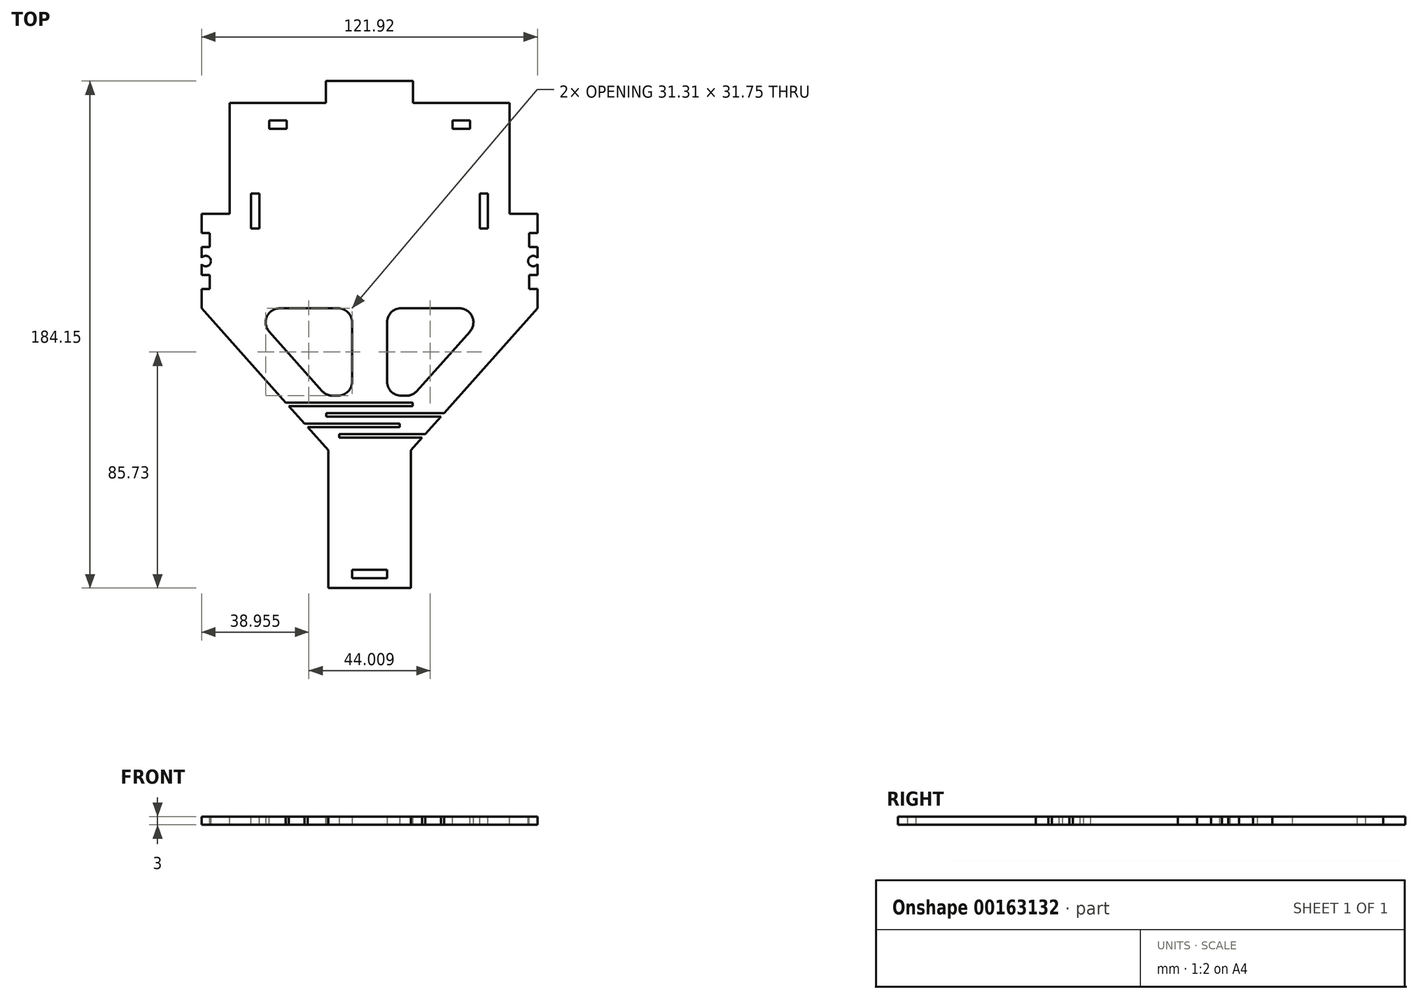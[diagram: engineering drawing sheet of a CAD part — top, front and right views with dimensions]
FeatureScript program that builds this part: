
annotation { "Feature Type Name" : "Feature", "Feature Type Description" : "" }
export const myFeature = defineFeature(function(context is Context, id is Id, definition is map)
    precondition{}
    {
        {
            var Q0;
            Q0=qCreatedBy(makeId("Top.planeOp"),FACE);
            var sketch = newSketch(context, id + "F0", { "sketchPlane" : qUnion([Q0])});
            skLineSegment(sketch, "E0.bottom", {"start": v(-50.8, 41.28) * mm, "end": v(50.8, 41.28) * mm});
            skLineSegment(sketch, "E0.top", {"start": v(-43.95, -41.28) * mm, "end": v(-6.35, -41.28) * mm});
            skLineSegment(sketch, "E0.left", {"start": v(-50.8, 41.28) * mm, "end": v(-50.8, -6.99) * mm});
            skLineSegment(sketch, "E0.right", {"start": v(50.8, 41.28) * mm, "end": v(50.8, -6.99) * mm});
            skPoint(sketch, "E0.middle", {"position": v(0, 0) * mm});
            skLineSegment(sketch, "E1.0", {"start": v(60.96, -6.98) * mm, "end": v(60.96, -41.28) * mm});
            skLineSegment(sketch, "E2.0", {"start": v(-50.8, -6.98) * mm, "end": v(50.8, -6.98) * mm, "construction": true});
            skLineSegment(sketch, "E3", {"start": v(50.8, -6.98) * mm, "end": v(60.96, -6.98) * mm});
            skPoint(sketch, "E4.orphan", {"position": v(50.8, -41.28) * mm});
            skLineSegment(sketch, "E5", {"start": v(-50.8, -6.98) * mm, "end": v(-60.96, -6.98) * mm});
            skPoint(sketch, "E6.orphan", {"position": v(-50.8, -41.28) * mm});
            skLineSegment(sketch, "E7", {"start": v(-60.96, -6.98) * mm, "end": v(-60.96, -41.28) * mm});
            skLineSegment(sketch, "E8", {"start": v(-60.96, -41.27) * mm, "end": v(-30.42, -75.57) * mm});
            skLineSegment(sketch, "E9", {"start": v(60.96, -41.28) * mm, "end": v(27.02, -79.38) * mm});
            skLineSegment(sketch, "E10", {"start": v(15, -92.88) * mm, "end": v(15, -142.88) * mm});
            skLineSegment(sketch, "E11", {"start": v(15, -142.88) * mm, "end": v(-15, -142.88) * mm});
            skLineSegment(sketch, "E12", {"start": v(-15, -142.88) * mm, "end": v(-15, -92.88) * mm});
            skLineSegment(sketch, "E13.0", {"start": v(-43.95, -41.28) * mm, "end": v(-15.67, -73.03) * mm});
            skLineSegment(sketch, "E14.0", {"start": v(43.95, -41.28) * mm, "end": v(15.67, -73.03) * mm});
            skLineSegment(sketch, "E15", {"start": v(-6.35, -41.28) * mm, "end": v(-6.35, -73.03) * mm});
            skLineSegment(sketch, "E16", {"start": v(6.35, -41.28) * mm, "end": v(6.35, -73.03) * mm});
            skLineSegment(sketch, "E17", {"start": v(-15.67, -73.03) * mm, "end": v(-6.35, -73.03) * mm});
            skLineSegment(sketch, "E18.trimOffspring", {"start": v(6.35, -73.03) * mm, "end": v(15.67, -73.03) * mm});
            skLineSegment(sketch, "E19.trimOffspring", {"start": v(6.35, -41.28) * mm, "end": v(43.95, -41.28) * mm});
            skLineSegment(sketch, "E20", {"start": v(-30.42, -75.57) * mm, "end": v(15.67, -75.57) * mm});
            skLineSegment(sketch, "E21", {"start": v(15.67, -76.84) * mm, "end": v(-29.29, -76.84) * mm});
            skLineSegment(sketch, "E22", {"start": v(27.02, -79.38) * mm, "end": v(-15.67, -79.38) * mm});
            skLineSegment(sketch, "E23", {"start": v(-15.67, -80.65) * mm, "end": v(25.9, -80.65) * mm});
            skLineSegment(sketch, "E24", {"start": v(15.67, -75.57) * mm, "end": v(15.67, -76.84) * mm});
            skLineSegment(sketch, "E25", {"start": v(-15.67, -79.38) * mm, "end": v(-15.67, -80.65) * mm});
            skLineSegment(sketch, "E26.0.1.0", {"start": v(-30.42, -83.19) * mm, "end": v(-23.63, -83.19) * mm, "construction": true});
            skLineSegment(sketch, "E26.0.1.1", {"start": v(11.01, -84.46) * mm, "end": v(-22.5, -84.46) * mm});
            skLineSegment(sketch, "E26.0.1.2", {"start": v(20.24, -87) * mm, "end": v(-11.01, -87) * mm});
            skLineSegment(sketch, "E26.0.1.3", {"start": v(-11.01, -88.27) * mm, "end": v(19.1, -88.27) * mm});
            skLineSegment(sketch, "E26.direction1", {"start": v(-29.29, -76.84) * mm, "end": v(-2.76, -76.84) * mm, "construction": true});
            skLineSegment(sketch, "E26.direction2", {"start": v(-29.29, -76.84) * mm, "end": v(-29.29, -84.46) * mm, "construction": true});
            skLineSegment(sketch, "E27", {"start": v(11.01, -83.19) * mm, "end": v(11.01, -84.46) * mm});
            skPoint(sketch, "E27.startSnap0", {"position": v(11.01, -73.03) * mm});
            skLineSegment(sketch, "E28", {"start": v(-11.01, -87) * mm, "end": v(-11.01, -88.27) * mm});
            skPoint(sketch, "E28.startSnap0", {"position": v(-11.01, -73.03) * mm});
            skLineSegment(sketch, "E29.trimOffspring", {"start": v(-23.63, -83.19) * mm, "end": v(11.01, -83.19) * mm});
            skLineSegment(sketch, "E30.trimOffspring", {"start": v(-29.29, -76.84) * mm, "end": v(-23.63, -83.19) * mm});
            skLineSegment(sketch, "E31.trimOffspring", {"start": v(-22.5, -84.46) * mm, "end": v(-15, -92.88) * mm});
            skLineSegment(sketch, "E32.trimOffspring", {"start": v(19.1, -88.27) * mm, "end": v(15, -92.88) * mm});
            skLineSegment(sketch, "E33.trimOffspring", {"start": v(25.9, -80.65) * mm, "end": v(20.24, -87) * mm});
            skSolve(sketch);
        }
        {
            var Q0;
            Q0 = qSketchRegion(id + "F0", true);
            extrude(context, id + "F1", {"entities" : qUnion([Q0]), "depth" : 3 * mm});
        }
        {
            var Q0;
            Q0=makeQuery(id+"F1.opExtrude","CAP_FACE",FACE,{"disambiguationData":[OSD([sQuery(id+"F0.wireOp",EDGE,"E0.bottom"),sQuery(id+"F0.wireOp",EDGE,"E0.top"),sQuery(id+"F0.wireOp",EDGE,"E0.left"),sQuery(id+"F0.wireOp",EDGE,"E0.right"),sQuery(id+"F0.wireOp",EDGE,"E1.0"),sQuery(id+"F0.wireOp",EDGE,"E3"),sQuery(id+"F0.wireOp",EDGE,"E5"),sQuery(id+"F0.wireOp",EDGE,"E7")])],"isStart":false});
            var sketch = newSketch(context, id + "F2", { "sketchPlane" : qUnion([Q0])});
            skLineSegment(sketch, "E34.0", {"start": v(-59.46, -6.98) * mm, "end": v(-59.46, -41.28) * mm, "construction": true});
            skLineSegment(sketch, "E35.0", {"start": v(59.46, -6.98) * mm, "end": v(59.46, -41.28) * mm, "construction": true});
            skPoint(sketch, "E36", {"position": v(-59.46, -24.13) * mm});
            skPoint(sketch, "E37", {"position": v(59.46, -24.13) * mm});
            skSolve(sketch);
        }
        {
            var Q0;
            Q0=sQuery(id+"F2.wireOp",VERTEX,"E36");
            var Q1;
            Q1=sQuery(id+"F2.wireOp",VERTEX,"E37");
            var Q2;
            Q2=makeQuery(id+"F1.opExtrude","SWEPT_BODY",BODY,{"disambiguationData":[OSD([sQuery(id+"F0.wireOp",EDGE,"E0.bottom"),sQuery(id+"F0.wireOp",EDGE,"E0.top"),sQuery(id+"F0.wireOp",EDGE,"E0.left"),sQuery(id+"F0.wireOp",EDGE,"E0.right"),sQuery(id+"F0.wireOp",EDGE,"E1.0"),sQuery(id+"F0.wireOp",EDGE,"E3"),sQuery(id+"F0.wireOp",EDGE,"E5"),sQuery(id+"F0.wireOp",EDGE,"E7")])]});
            hole(context, id + "F3", {"style" : HoleStyle.SIMPLE, "endStyle" : HoleEndStyle.THROUGH, "standardTappedOrClearance" : lookupTablePath({ "standard" : "ANSI", "fit" : "Normal (ASME)", "size" : "#6", "type" : "Clearance" }), "standardBlindInLast" : lookupTablePath({ "fit" : "Free", "standard" : "ANSI", "size" : "#6", "type" : "Clearance" }), "holeDiameter" : 3.8 * mm, "locations" : qUnion([Q0, Q1]), "scope" : qUnion([Q2]), "isTappedThrough" : true});
        }
        {
            var Q0;
            Q0=makeQuery(id+"F1.opExtrude","CAP_FACE",FACE,{"disambiguationData":[OSD([sQuery(id+"F0.wireOp",EDGE,"E0.bottom"),sQuery(id+"F0.wireOp",EDGE,"E0.top"),sQuery(id+"F0.wireOp",EDGE,"E0.left"),sQuery(id+"F0.wireOp",EDGE,"E0.right"),sQuery(id+"F0.wireOp",EDGE,"E1.0"),sQuery(id+"F0.wireOp",EDGE,"E3"),sQuery(id+"F0.wireOp",EDGE,"E5"),sQuery(id+"F0.wireOp",EDGE,"E7")])],"isStart":false});
            var sketch = newSketch(context, id + "F4", { "sketchPlane" : qUnion([Q0])});
            skLineSegment(sketch, "E38.0", {"start": v(-57.96, -6.98) * mm, "end": v(-57.96, -34.93) * mm, "construction": true});
            skLineSegment(sketch, "E39", {"start": v(-60.96, -29.21) * mm, "end": v(-57.96, -29.21) * mm});
            skLineSegment(sketch, "E40", {"start": v(-60.96, -34.3) * mm, "end": v(-57.96, -34.3) * mm});
            skLineSegment(sketch, "E41", {"start": v(-60.96, -19.05) * mm, "end": v(-57.96, -19.05) * mm});
            skLineSegment(sketch, "E42", {"start": v(-60.96, -13.97) * mm, "end": v(-57.96, -13.97) * mm});
            skLineSegment(sketch, "E43", {"start": v(-57.96, -13.97) * mm, "end": v(-57.96, -19.05) * mm});
            skLineSegment(sketch, "E44", {"start": v(-57.96, -29.21) * mm, "end": v(-57.96, -34.3) * mm});
            skLineSegment(sketch, "E45", {"start": v(-60.96, -29.21) * mm, "end": v(-60.96, -34.3) * mm});
            skLineSegment(sketch, "E46", {"start": v(-60.96, -13.97) * mm, "end": v(-60.96, -19.05) * mm});
            skLineSegment(sketch, "E47.0", {"start": v(57.96, -34.93) * mm, "end": v(57.96, -6.98) * mm, "construction": true});
            skLineSegment(sketch, "E48", {"start": v(60.96, -19.05) * mm, "end": v(57.96, -19.05) * mm});
            skLineSegment(sketch, "E49", {"start": v(60.96, -13.97) * mm, "end": v(57.96, -13.97) * mm});
            skLineSegment(sketch, "E50", {"start": v(60.96, -29.21) * mm, "end": v(57.96, -29.21) * mm});
            skLineSegment(sketch, "E51", {"start": v(60.96, -34.3) * mm, "end": v(57.96, -34.3) * mm});
            skLineSegment(sketch, "E52", {"start": v(57.96, -34.3) * mm, "end": v(57.96, -29.21) * mm});
            skLineSegment(sketch, "E53", {"start": v(57.96, -19.05) * mm, "end": v(57.96, -13.97) * mm});
            skLineSegment(sketch, "E54", {"start": v(60.96, -19.05) * mm, "end": v(60.96, -13.97) * mm});
            skLineSegment(sketch, "E55", {"start": v(60.96, -34.3) * mm, "end": v(60.96, -29.21) * mm});
            skLineSegment(sketch, "E56.bottom", {"start": v(-50.8, 41.28) * mm, "end": v(-15.8, 41.28) * mm});
            skLineSegment(sketch, "E56.top", {"start": v(-50.8, 33.28) * mm, "end": v(-15.8, 33.28) * mm});
            skLineSegment(sketch, "E56.left", {"start": v(-50.8, 41.28) * mm, "end": v(-50.8, 33.28) * mm});
            skLineSegment(sketch, "E56.right", {"start": v(-15.8, 41.28) * mm, "end": v(-15.8, 33.28) * mm});
            skLineSegment(sketch, "E57.bottom", {"start": v(50.8, 41.28) * mm, "end": v(15.8, 41.28) * mm});
            skLineSegment(sketch, "E57.top", {"start": v(50.8, 33.28) * mm, "end": v(15.8, 33.28) * mm});
            skLineSegment(sketch, "E57.left", {"start": v(50.8, 41.28) * mm, "end": v(50.8, 33.28) * mm});
            skLineSegment(sketch, "E57.right", {"start": v(15.8, 41.28) * mm, "end": v(15.8, 33.28) * mm});
            skLineSegment(sketch, "E58.bottom", {"start": v(-36.47, 26.93) * mm, "end": v(-30.12, 26.93) * mm});
            skLineSegment(sketch, "E58.top", {"start": v(-36.47, 23.93) * mm, "end": v(-30.12, 23.93) * mm});
            skLineSegment(sketch, "E58.left", {"start": v(-36.47, 26.93) * mm, "end": v(-36.47, 23.93) * mm});
            skLineSegment(sketch, "E58.right", {"start": v(-30.12, 26.93) * mm, "end": v(-30.12, 23.93) * mm});
            skPoint(sketch, "E58.middle", {"position": v(-33.3, 25.43) * mm});
            skPoint(sketch, "E58.middle.positionSnap0", {"position": v(-33.3, 33.28) * mm});
            skPoint(sketch, "E58.centerSnap0", {"position": v(-33.3, 33.28) * mm});
            skLineSegment(sketch, "E59.bottom", {"start": v(30.13, 26.93) * mm, "end": v(36.48, 26.93) * mm});
            skLineSegment(sketch, "E59.top", {"start": v(30.13, 23.93) * mm, "end": v(36.48, 23.93) * mm});
            skLineSegment(sketch, "E59.left", {"start": v(30.13, 26.93) * mm, "end": v(30.13, 23.93) * mm});
            skLineSegment(sketch, "E59.right", {"start": v(36.48, 26.93) * mm, "end": v(36.48, 23.93) * mm});
            skPoint(sketch, "E59.middle", {"position": v(33.3, 25.43) * mm});
            skPoint(sketch, "E59.middle.positionSnap0", {"position": v(-30.12, 25.43) * mm});
            skPoint(sketch, "E59.middle.positionSnap1", {"position": v(33.3, 33.28) * mm});
            skPoint(sketch, "E59.centerSnap0", {"position": v(-30.12, 25.43) * mm});
            skPoint(sketch, "E59.centerSnap1", {"position": v(33.3, 33.28) * mm});
            skLineSegment(sketch, "E60", {"start": v(0, 0) * mm, "end": v(0, -44.7) * mm, "construction": true});
            skLineSegment(sketch, "E61.bottom", {"start": v(40, -12.28) * mm, "end": v(43, -12.28) * mm});
            skLineSegment(sketch, "E61.top", {"start": v(40, 0.42) * mm, "end": v(43, 0.42) * mm});
            skLineSegment(sketch, "E61.left", {"start": v(40, -12.28) * mm, "end": v(40, 0.42) * mm});
            skLineSegment(sketch, "E61.right", {"start": v(43, -12.28) * mm, "end": v(43, 0.42) * mm});
            skLineSegment(sketch, "E62.bottom", {"start": v(-43, -12.28) * mm, "end": v(-40, -12.28) * mm});
            skLineSegment(sketch, "E62.top", {"start": v(-43, 0.42) * mm, "end": v(-40, 0.42) * mm});
            skLineSegment(sketch, "E62.left", {"start": v(-43, -12.28) * mm, "end": v(-43, 0.42) * mm});
            skLineSegment(sketch, "E62.right", {"start": v(-40, -12.28) * mm, "end": v(-40, 0.42) * mm});
            skLineSegment(sketch, "E63.bottom", {"start": v(6.35, -136.3) * mm, "end": v(-6.35, -136.3) * mm});
            skLineSegment(sketch, "E63.top", {"start": v(6.35, -139.3) * mm, "end": v(-6.35, -139.3) * mm});
            skLineSegment(sketch, "E63.left", {"start": v(6.35, -136.3) * mm, "end": v(6.35, -139.3) * mm});
            skLineSegment(sketch, "E63.right", {"start": v(-6.35, -136.3) * mm, "end": v(-6.35, -139.3) * mm});
            skPoint(sketch, "E63.middle", {"position": v(0, -137.8) * mm});
            skLineSegment(sketch, "E64.0", {"start": v(15, -137.8) * mm, "end": v(-15, -137.8) * mm, "construction": true});
            skSolve(sketch);
        }
        {
            var Q0;
            Q0 = qSketchRegion(id + "F4", true);
            extrude(context, id + "F5", {"entities" : qUnion([Q0]), "operationType" : NewBodyOperationType.REMOVE, "endBound" : BoundingType.THROUGH_ALL, "oppositeDirection" : true, "depth" : 25.4 * mm});
        }
        {
            var Q0;
            Q0=makeQuery(id+"F1.opExtrude","SWEPT_EDGE",EDGE,{"disambiguationData":[OSD([sQuery(id+"F0.wireOp",EDGE,"E0.top"),sQuery(id+"F0.wireOp",EDGE,"E13.0")])]});
            var Q1;
            Q1=makeQuery(id+"F1.opExtrude","SWEPT_EDGE",EDGE,{"disambiguationData":[OSD([sQuery(id+"F0.wireOp",EDGE,"E0.top"),sQuery(id+"F0.wireOp",EDGE,"E15")])]});
            var Q2;
            Q2=makeQuery(id+"F1.opExtrude","SWEPT_EDGE",EDGE,{"disambiguationData":[OSD([sQuery(id+"F0.wireOp",EDGE,"E14.0"),sQuery(id+"F0.wireOp",EDGE,"E19.trimOffspring")])]});
            var Q3;
            Q3=makeQuery(id+"F1.opExtrude","SWEPT_EDGE",EDGE,{"disambiguationData":[OSD([sQuery(id+"F0.wireOp",EDGE,"E16"),sQuery(id+"F0.wireOp",EDGE,"E19.trimOffspring")])]});
            var Q4;
            Q4=makeQuery(id+"F1.opExtrude","SWEPT_EDGE",EDGE,{"disambiguationData":[OSD([sQuery(id+"F0.wireOp",EDGE,"E14.0"),sQuery(id+"F0.wireOp",EDGE,"E18.trimOffspring")])]});
            var Q5;
            Q5=makeQuery(id+"F1.opExtrude","SWEPT_EDGE",EDGE,{"disambiguationData":[OSD([sQuery(id+"F0.wireOp",EDGE,"E13.0"),sQuery(id+"F0.wireOp",EDGE,"E17")])]});
            var Q6;
            Q6=makeQuery(id+"F1.opExtrude","SWEPT_EDGE",EDGE,{"disambiguationData":[OSD([sQuery(id+"F0.wireOp",EDGE,"E15"),sQuery(id+"F0.wireOp",EDGE,"E17")])]});
            var Q7;
            Q7=makeQuery(id+"F1.opExtrude","SWEPT_EDGE",EDGE,{"disambiguationData":[OSD([sQuery(id+"F0.wireOp",EDGE,"E16"),sQuery(id+"F0.wireOp",EDGE,"E18.trimOffspring")])]});
            fillet(context, id + "F6", {"entities" : qUnion([Q0, Q1, Q2, Q3, Q4, Q5, Q6, Q7]), "radius" : 5.08 * mm, "tangentPropagation" : true, "allowEdgeOverflow" : false});
        }
    });
